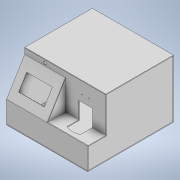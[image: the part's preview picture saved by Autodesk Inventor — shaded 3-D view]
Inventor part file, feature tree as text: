
AUTODESK INVENTOR PART (.ipt)
format: ipt  version: 2020 (Build 240168000, 168)  size: 479,744 bytes
history: native  units: in
note: dims shown in document units (in); Inventor stores cm internally (conversion verified against a paired STEP export)
features: extrude x16, plane x16, split x13, sketch x13, boolean_combine x4, other x4
ambient origin geometry x8: Origin, YZ Plane, XZ Plane, XY Plane, X Axis, Y Axis, Z Axis, Center Point
bodies: Solid2 (feature_tree), Solid3 (feature_tree), Solid4 (feature_tree), Solid6 (feature_tree), Solid37 (feature_tree), Solid38 (feature_tree), Solid39 (feature_tree), Solid40 (feature_tree), Solid42 (feature_tree), Solid43 (feature_tree), Solid44 (feature_tree), Solid45 (feature_tree), Solid47 (feature_tree), Solid53 (feature_tree), Solid58 (feature_tree), Solid61 (feature_tree), Solid63 (feature_tree), Solid64 (feature_tree)
feature tree (66):
  extrude  "Extrusion4"  Depth=6.2992in
  extrude  "Extrusion5"  Depth=11.811in
  plane  "Work Plane1"
  split  "Split1"
  extrude  "Extrusion6"  Depth=5.1181in TaperAngle=0.0deg
  extrude  "Extrusion7"  TaperAngle=0.0deg  [1 undecoded]
  plane  "Work Plane2"
  extrude  "Extrusion8"  TaperAngle=0.0deg  [1 undecoded]
  extrude  "Extrusion9"  Depth=11.811in TaperAngle=0.0deg
  extrude  "Extrusion10"  TaperAngle=0.0deg  [1 undecoded]
  plane  "Work Plane3"
  plane  "Work Plane17"
  split  "Split19"
  extrude  "Extrusion19"  Depth=10.4331in
  plane  "Work Plane18"
  split  "Split20"
  plane  "Work Plane19"
  split  "Split21"
  extrude  "Extrusion20"  Depth=5.1181in
  sketch  "Sketch27"  dims[d44=24.8031in d45=0.0in d46=0.0in]
  plane  "Work Plane20"
  extrude  "Extrusion21"  Depth=1.5748in
  split  "Split22"
  plane  "Work Plane21"
  split  "Split23"
  boolean_combine  "Combine5"
  extrude  "Extrusion22"  Depth=0.1969in
  plane  "Work Plane22"
  boolean_combine  "Combine6"
  extrude  "Extrusion23"  Depth=6.2992in
  plane  "Work Plane23"
  extrude  "Extrusion24"  Depth=19.4882in
  split  "Split24"
  extrude  "Extrusion25"  Depth=10.4331in TaperAngle=0.0deg
  plane  "Work Plane24"
  split  "Split25"
  plane  "Work Plane25"
  plane  "Work Plane26"
  split  "Split27"
  split  "Split28"
  extrude  "Extrusion27"  TaperAngle=0.0deg  [1 undecoded]
  plane  "Work Plane27"
  split  "Split29"
  plane  "Work Plane31"
  split  "Split31"
  boolean_combine  "Combine10"
  sketch  "Sketch34"  dims[d104=-0.1969in d105=19.4882in d106=10.4331in d107=0.0in d108=0.0in d109=0.0in d110=0.1969in d111=0.0in d112=11.811in d113=0.0in d114=7.5197in d115=4.5276in d116=5.9055in d117=11.811in d118=0.0in d119=0.1969in d120=0.0in d121=24.8031in d122=0.0in d123=0.1969in d124=16.5354in d125=0.0in d126=0.0in d127=0.0in d130=-0.1969in d131=0.1969in d132=0.0in d133=0.0in d136=1.9685in d137=-1.5748in d138=0.1969in d139=0.0in d140=-0.1969in d63=0.0197in d64=0.0344in d65=0.0197in d66=0.0344in]
  boolean_combine  "Combine11"
  extrude  "Extrusion28"  TaperAngle=0.0deg  [1 undecoded]
  plane  "Work Plane32"
  split  "Split32"
  sketch  "Sketch7"  dims[d13=23.622in d14=6.2992in]
  sketch  "Sketch8"  dims[d15=0.1969in d16=0.0in d17=11.811in]
  sketch  "Sketch11"  dims[d18=0.1969in d19=5.1181in d20=0.0in]
  sketch  "Sketch13"  dims[d21=0.0in d24=0.0in d25=0.0in]
  sketch  "Sketch25"  dims[d30=0.1969in d31=0.0in d32=0.0in]
  sketch  "Sketch26"  dims[d34=11.811in d35=0.0in d37=5.4469in d38=0.0in]
  sketch  "Sketch28"  dims[d82=11.811in d83=10.4331in]
  sketch  "Sketch29"  dims[d84=3.937in d85=5.1181in]
  sketch  "Sketch30"  dims[d93=0.1969in d94=1.5748in]
  sketch  "Sketch31"  dims[d95=0.9055in d100=0.1969in]
  sketch  "Sketch33"  dims[d101=0.1969in d102=6.2992in]
  other  "Màn hình"
  other  "Đáy"
  other  "Má trái"
  other  "Camera"
note: 5 required parameter values undecoded (feature->parameter linkage not recoverable at this tier; creation-order binding heuristic only, values carry confidence <= 0.55)
